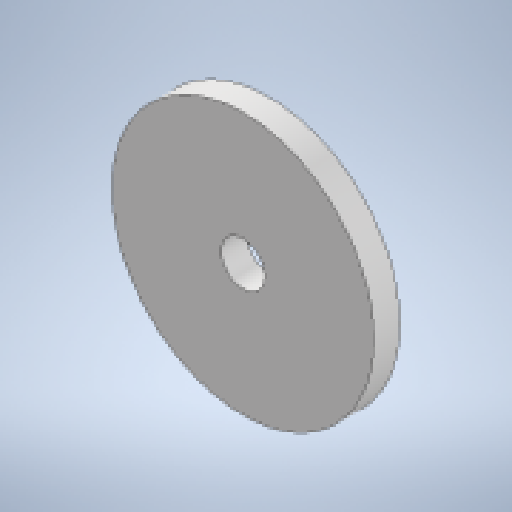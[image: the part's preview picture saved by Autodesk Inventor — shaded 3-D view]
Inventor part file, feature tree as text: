
AUTODESK INVENTOR PART (.ipt)
format: ipt  version: 2023 (Build 270158000, 158)  size: 183,296 bytes
history: native  units: mm
features: extrude x5, sketch x5, projected_geometry x4, other x1
ambient origin geometry x8: Origin, YZ Plane, XZ Plane, XY Plane, X Axis, Y Axis, Z Axis, Center Point
bodies: Body1 (feature_tree)
feature tree (15):
  other  "實體1"
  extrude  "擠出1"  Depth=5.0mm
  extrude  "擠出2"  Depth=30.0mm
  extrude  "擠出3"  Depth=3.0mm TaperAngle=0.0deg
  extrude  "擠出5"  Depth=3.0mm TaperAngle=0.0deg
  extrude  "擠出6"  Depth=17.5mm TaperAngle=0.0deg
  sketch  "草圖1"
  sketch  "草圖2"
  projected_geometry  "投影迴路1"
  sketch  "草圖3"
  projected_geometry  "投影迴路2"
  sketch  "草圖5"
  projected_geometry  "投影迴路4"
  sketch  "草圖6"
  projected_geometry  "投影迴路5"
